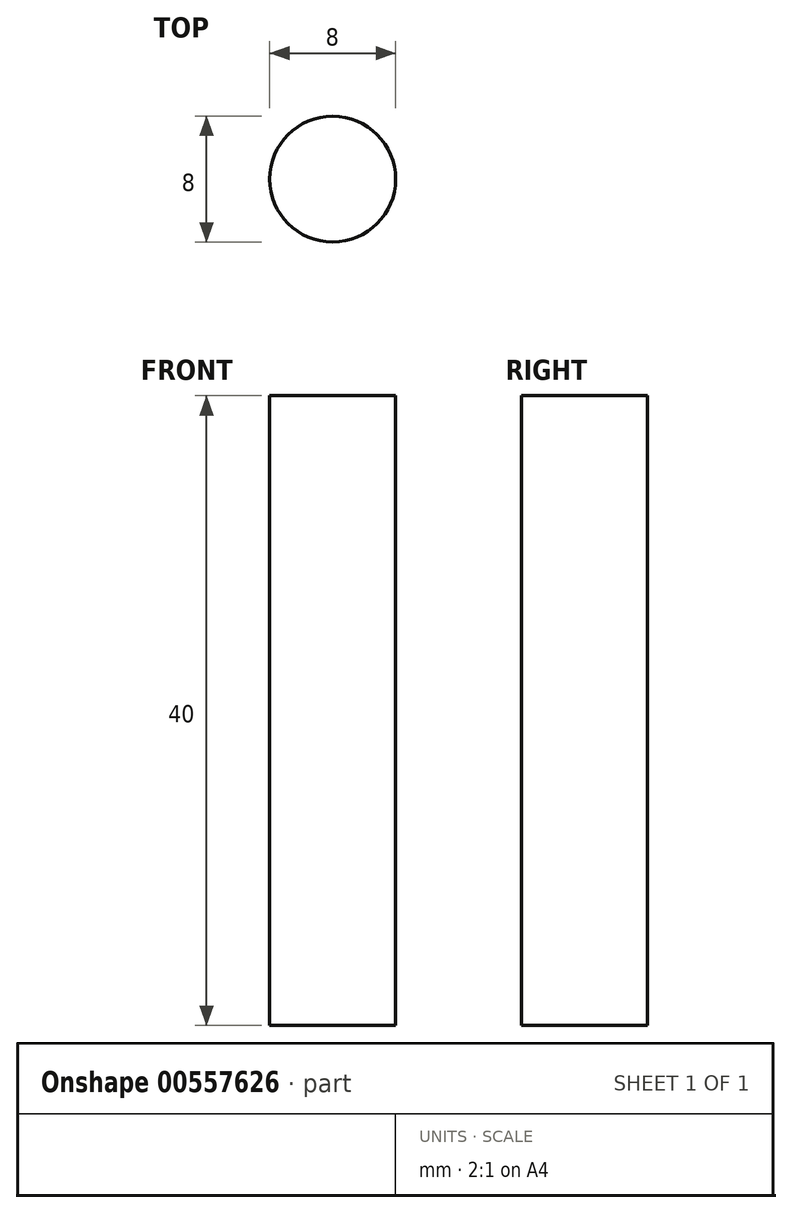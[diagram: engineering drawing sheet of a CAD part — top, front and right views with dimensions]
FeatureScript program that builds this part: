
annotation { "Feature Type Name" : "Feature", "Feature Type Description" : "" }
export const myFeature = defineFeature(function(context is Context, id is Id, definition is map)
    precondition{}
    {
        {
            var Q0;
            Q0=qCreatedBy(makeId("Top.planeOp"),FACE);
            var sketch = newSketch(context, id + "F0", { "sketchPlane" : qUnion([Q0])});
            skCircle(sketch, "E0", {"center": v(0, 0) * mm, "radius": 4 * mm});
            skSolve(sketch);
        }
        {
            var Q0;
            Q0 = qSketchRegion(id + "F0", true);
            extrude(context, id + "F1", {"entities" : qUnion([Q0]), "depth" : 40 * mm, "offsetDistance" : 25 * mm});
        }
    });
